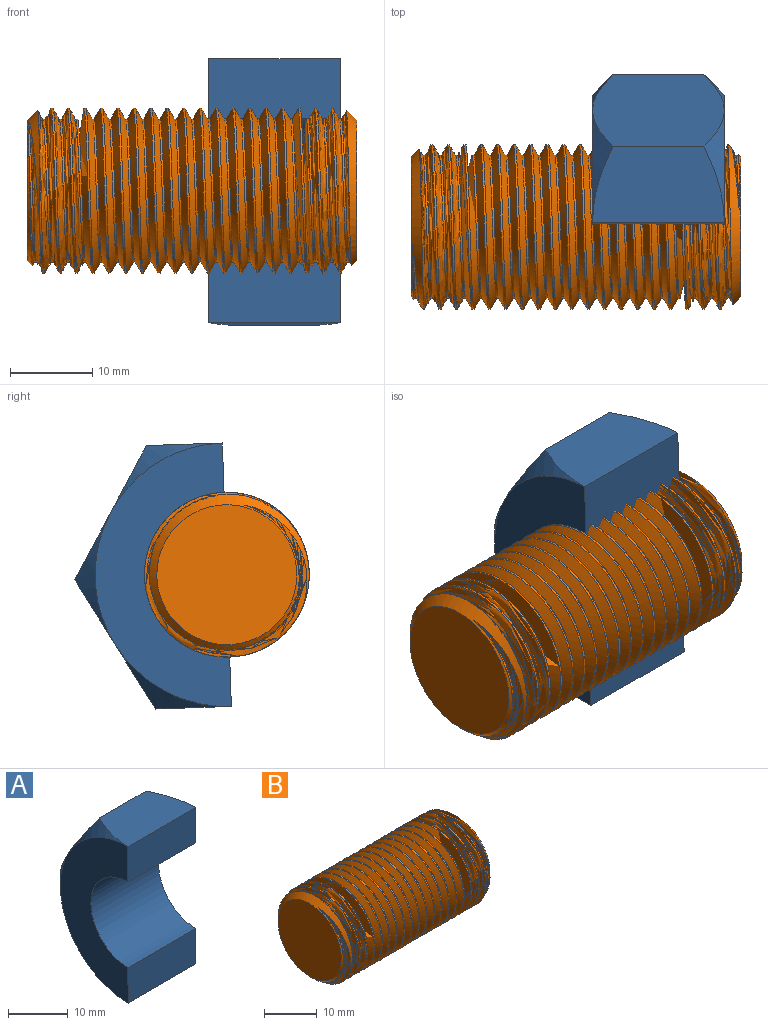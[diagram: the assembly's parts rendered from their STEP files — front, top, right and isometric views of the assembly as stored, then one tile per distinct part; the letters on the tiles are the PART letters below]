
ASSEMBLY  parts=2 mates=1
PART A: 15 faces, bbox 16x18.5x37 mm
  f0: plane 16x7.23mm, normal (0,-1,0), area 115.7mm2, adj f9,f11,f12,f13
  f1: cone r=18.5mm half-angle=45deg, axis (-1,0,0), area 19.5mm2, adj f2,f4,f13
  f2: plane 16.01x16mm, normal (0,0.87,-0.5), area 264.2mm2, adj f1,f3,f4,f6,f7,f8
  f3: cone r=18.5mm half-angle=45deg, axis (-1,0,0), area 19.5mm2, adj f2,f6,f13
  f4: plane 16.01x16mm, normal (0,0.87,0.5), area 264.2mm2, adj f1,f2,f5,f8,f9,f10
  f5: cone r=18.5mm half-angle=45deg, axis (-1,0,0), area 19.5mm2, adj f4,f9,f13
  f6: plane 16.01x9.24mm, normal (0,0,-1), area 132.1mm2, adj f2,f3,f7,f14
  f7: cone r=18.5mm half-angle=45deg, axis (1,0,0), area 19.5mm2, adj f2,f6,f12
  f8: cone r=18.5mm half-angle=45deg, axis (1,0,0), area 19.5mm2, adj f2,f4,f12
  f9: plane 16.01x9.24mm, normal (0,0,1), area 132.1mm2, adj f0,f4,f5,f10
  f10: cone r=18.5mm half-angle=45deg, axis (1,0,0), area 19.5mm2, adj f4,f9,f12
  f11: cylinder r=8.77mm len=17.53mm, axis (-1,0,0), area 440.7mm2, adj f0,f12,f13,f14
  f12: plane 32x16mm, normal (-1,0,0), area 281.4mm2, adj f0,f7,f8,f10,f11,f14
  f13: plane 32x16mm, normal (1,0,0), area 281.4mm2, adj f0,f1,f3,f5,f11,f14
  f14: plane 16x7.23mm, normal (0,-1,0), area 115.7mm2, adj f6,f11,f12,f13
PART B: 8 faces, bbox 41.8x23.1x20 mm
  f0: plane 17x17mm, normal (1,0,0), area 227mm2, adj f3
  f1: cylinder r=10mm len=37mm, axis (-1,0,0), area 568.4mm2, adj f3,f4,f5,f7
  f2: plane 17x17mm, normal (-1,0,0), area 227mm2, adj f4
  f3: cone r=10mm half-angle=45deg, axis (-1,0,0), area 68.4mm2, adj f0,f1,f5,f6,f7
  f4: cone r=8.5mm half-angle=45deg, axis (1,0,0), area 68.4mm2, adj f1,f2,f5,f6,f7
  f5: bspline ~40.75x23.09mm, area 1706.6mm2, adj f1,f3,f4,f6
  f6: cylinder r=8.7mm len=39.6mm, axis (-1,0,0), area 259.2mm2, adj f3,f4,f5,f7
  f7: bspline ~40.75x23.09mm, area 1686.1mm2, adj f1,f3,f4,f6
PLACE A rot(axis=(-1,0,0),2deg) t=(0.57,-3.23,6.79)mm
PLACE B t=(-9.44,-3.23,6.79)mm fixed
MATE cylindrical A.f1 <-> B.f1  axis (1,0,0) through (8.57,-3.23,6.79)mm
